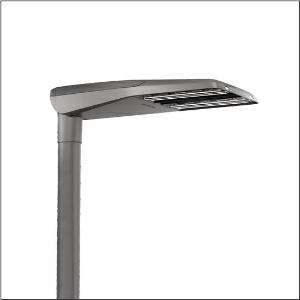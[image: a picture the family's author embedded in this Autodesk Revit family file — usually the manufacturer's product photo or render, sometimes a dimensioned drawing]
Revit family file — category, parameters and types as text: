
# Revit family: streetlight_sl_11_iq_midi___st1_0a_5xc3m41f08me_932e
name_source: partatom
category: Lighting Fixtures
units: mm (PartAtom-declared; Revit-internal decimal feet)

## family parameters
Cut with Voids When Loaded = No
Host = Face
Light Source = No
Part Type = Normal
Room Calculation Point = No
Round Connector Dimension = Use Diameter
Shared = No

## types (1)
- --- (1 x LED, 18310 lm, 124.7 W, 4000K)
    Apparent Load = 125 VA
    CIE Flux Codes = 33 66 96 100 100
    Color Rendering = 70
    Color Temperature = 4000K
    Default Elevation = 1800 mm
    Description = Streetlight SL 11 iQ midi, mast luminaire, primary light control with 3 zone facetted reflector, of plastic, silver coated, highly specular, primary optical cover: cover, of PMMA, transparent, light distribution: ST1.0a, light emission: direct distribution, primary light characteristic: asymmetric, installation type: post-top, side-entry, LED, High Power LED, rated luminous flux: 18.310lm, luminous efficacy: 147lm/W, light colour: 740, colour temperature: 4000K, control: optimised constant luminous flux control (CLO 2.0), Street-Remote, Desk-Remote (wireless, voltage-free reading and setting of iQ features in the workshop via application-optimized NFC function/RFID function), Light-Fading, Smart-Wire, Night-Set, Lumen-Switch, Temp-Guard, Auto-Match, with cable H07RN-F 5x 1.5mm², mains connection: 230..240V, AC, 50/60Hz, connection cable pre-assembled, cable length: 12,5m, start of lifetime: 125W, end of service life: 132W, reduction: 57W, luminaire housing, of diecast aluminium, powder-coated, Siteco® metallic grey (DB 702S), please order mast flange separately, inclination adjustable without tools: 0°, 5°, 10°, 15° (post-top) | 0°, -5°, -10°, -15° (side-entry), sealing non-destructively replaceable, multi-level sealing system, length: 780mm, width: 376mm, height: 118mm, mast flange for spigot size: 42mm (side-entry): 5XC10008XM4, 60/48mm (side-entry/post-top): 5XC10108XM2, 76/60mm (side-entry/post-top): 5XC10108XM1, equipment: Power, protection rating (complete): IP66, insulation class (complete): insulation class II (safety insulation), certification: CE, ENEC, VDE, impact resistance: IK09, permissible operating ambient temperature for outdoor applications: -25..+50°C, standard-compliant lighting for roads and squares, Environmental Product Declaration (EPD) tested and certified by an independent institute, packaging unit: 1 piece

Light Distribution: ST1.0a
    Height = 118 mm
    Lamp = 1 x LED
    Lamp Light Flux = 18310 lm
    Lamp Power = 124.7 W
    Lamp count = 1
    Length = 780 mm
    Luminous efficacy = 147 lm/W
    Manufacturer = Siteco
    ModVariant = No
    Model = 5XC3M41F08ME
    Number of Poles = 1
    OnlyDefault = Yes
    Power Factor = 1
    Product Name = Streetlight SL 11 iQ midi | ST1.0a
    Product group = mast luminaire | pylon top
    ProductGroupID = 6100
    Protection Class = Protection class II
    Protection Degree = IP 66
    RLX_Detail_Level = 1
    RLX_Emergency_Light_Flux = 0 lm
    RLX_Emergency_Type = 0
    RLX_Emergency_Type_DB = No
    RlxData = <blob elided: 70193 chars, md5=37cc9291>
    Socket = socket
    Standby Power = 0 W
    System Light Flux = 18310 lm
    System Power = 125 W
    Type Comments = factory setting: luminous flux: 100 % | dim-lin: 254 | 557 mA
    Type Image = l_1005960.jpg
    URL = http://relux.com
    VarID = @adj_039531
    Voltage = 0 V
    Weight = 0.00 kg
    Width = 376 mm

## geometry (parser evidence)
native form markers: Blend x4, Sweep x11
no freeform markers — native parametric forms only
